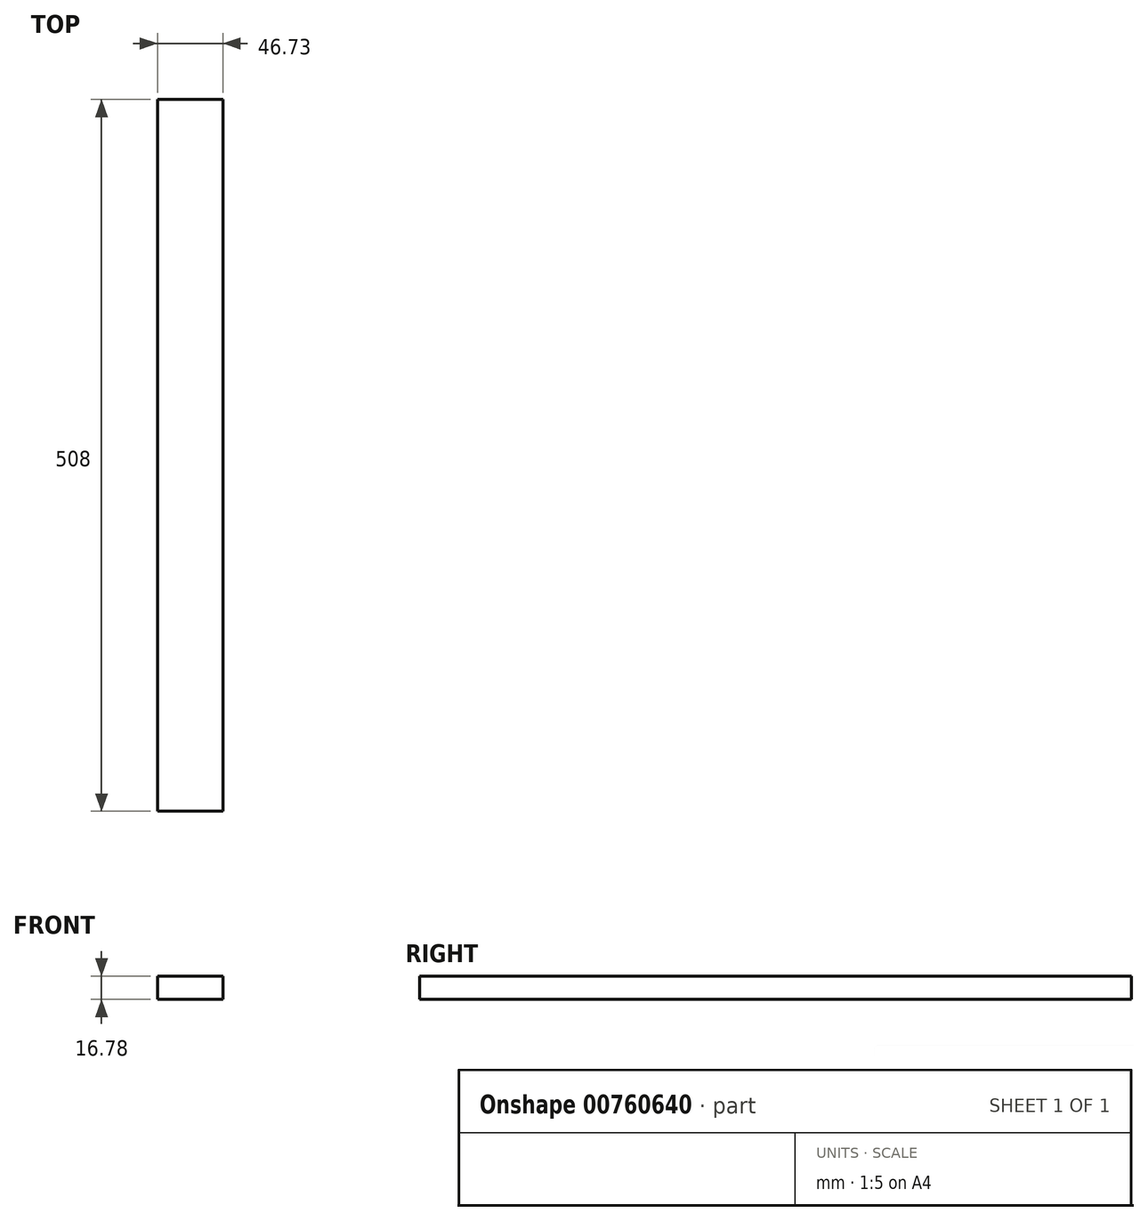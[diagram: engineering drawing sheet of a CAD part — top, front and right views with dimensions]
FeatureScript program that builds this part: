
annotation { "Feature Type Name" : "Feature", "Feature Type Description" : "" }
export const myFeature = defineFeature(function(context is Context, id is Id, definition is map)
    precondition{}
    {
        {
            var Q0;
            Q0=qCreatedBy(makeId("Front.planeOp"),FACE);
            var sketch = newSketch(context, id + "F0", { "sketchPlane" : qUnion([Q0])});
            skLineSegment(sketch, "E0.bottom", {"start": v(-36.14, 29.56) * mm, "end": v(13.06, 29.56) * mm});
            skLineSegment(sketch, "E0.top", {"start": v(-36.14, 0) * mm, "end": v(13.06, 0) * mm});
            skLineSegment(sketch, "E0.left", {"start": v(-36.14, 29.56) * mm, "end": v(-36.14, 0) * mm});
            skLineSegment(sketch, "E0.right", {"start": v(13.06, 29.56) * mm, "end": v(13.06, 0) * mm});
            skLineSegment(sketch, "E1.bottom", {"start": v(-9.25, 34.33) * mm, "end": v(-55.98, 34.33) * mm});
            skLineSegment(sketch, "E1.top", {"start": v(-9.25, 51.11) * mm, "end": v(-55.98, 51.11) * mm});
            skLineSegment(sketch, "E1.left", {"start": v(-9.25, 34.33) * mm, "end": v(-9.25, 51.11) * mm});
            skLineSegment(sketch, "E1.right", {"start": v(-55.98, 34.33) * mm, "end": v(-55.98, 51.11) * mm});
            skCircle(sketch, "E2", {"center": v(39.77, 47.5) * mm, "radius": 18.58 * mm});
            skSolve(sketch);
        }
        {
            var Q0;
            Q0=makeQuery(id+"F0.imprint","IMPRINT",FACE,{"disambiguationData":[TD([[makeQuery(id+"F0.imprint","IMPRINT",EDGE,{"derivedFrom":sQuery(id+"F0.wireOp",EDGE,"E1.bottom")}),-1.0]])]});
            extrude(context, id + "F1", {"entities" : qUnion([Q0]), "depth" : 508 * mm, "offsetDistance" : 25.4 * mm});
        }
    });
